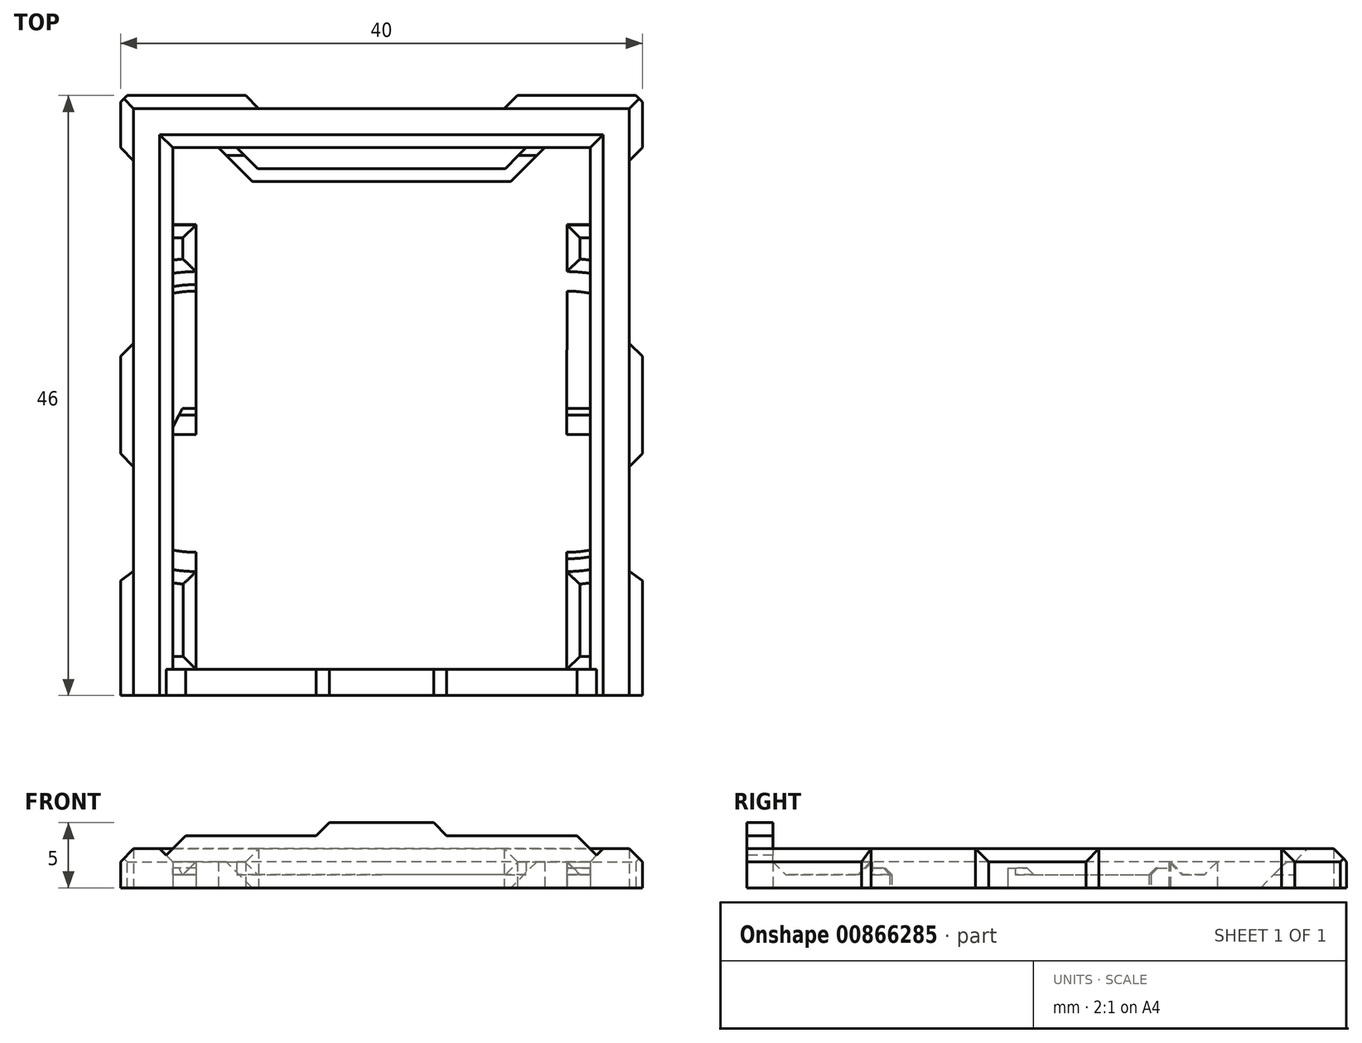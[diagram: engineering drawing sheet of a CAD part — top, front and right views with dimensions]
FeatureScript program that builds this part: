
annotation { "Feature Type Name" : "Feature", "Feature Type Description" : "" }
export const myFeature = defineFeature(function(context is Context, id is Id, definition is map)
    precondition{}
    {
        {
            var Q0;
            Q0=qCreatedBy(makeId("Top.planeOp"),FACE);
            var sketch = newSketch(context, id + "F0", { "sketchPlane" : qUnion([Q0])});
            skLineSegment(sketch, "E0", {"start": v(-16, -21) * mm, "end": v(-20, -21) * mm});
            skLineSegment(sketch, "E1", {"start": v(0, -19) * mm, "end": v(-16, -19) * mm});
            skLineSegment(sketch, "E2", {"start": v(-16, -21) * mm, "end": v(-16, -19) * mm});
            skLineSegment(sketch, "E3", {"start": v(-16, -19) * mm, "end": v(-16, 21) * mm});
            skLineSegment(sketch, "E4", {"start": v(-20, -21) * mm, "end": v(-20, -12.2) * mm});
            skLineSegment(sketch, "E5", {"start": v(-20, 21) * mm, "end": v(-20, 25) * mm});
            skLineSegment(sketch, "E6", {"start": v(-10.41, 25) * mm, "end": v(-20, 25) * mm});
            skLineSegment(sketch, "E7", {"start": v(-10.41, 25) * mm, "end": v(-9.41, 24) * mm});
            skLineSegment(sketch, "E8", {"start": v(-20, -12.2) * mm, "end": v(-19, -11.46) * mm});
            skLineSegment(sketch, "E9", {"start": v(-20, 21) * mm, "end": v(-19, 20) * mm});
            skLineSegment(sketch, "E10", {"start": v(-19, -11.46) * mm, "end": v(-19, -3.46) * mm});
            skLineSegment(sketch, "E11", {"start": v(-20, 5) * mm, "end": v(-19, 6) * mm});
            skLineSegment(sketch, "E12", {"start": v(-20, -2.46) * mm, "end": v(-19, -3.46) * mm});
            skLineSegment(sketch, "E13", {"start": v(-20, 5) * mm, "end": v(-20, -2.46) * mm});
            skLineSegment(sketch, "E14", {"start": v(-19, 6) * mm, "end": v(-19, 20) * mm});
            skLineSegment(sketch, "E15", {"start": v(-16, -21) * mm, "end": v(-14, -21) * mm});
            skLineSegment(sketch, "E16", {"start": v(0, -21) * mm, "end": v(-5, -21) * mm});
            skLineSegment(sketch, "E17", {"start": v(-5, -21) * mm, "end": v(-5, -19) * mm});
            skPoint(sketch, "E18", {"position": v(-9.91, 24.5) * mm});
            skLineSegment(sketch, "E19", {"start": v(-9.5, 19.4) * mm, "end": v(-11.1, 21) * mm});
            skLineSegment(sketch, "E20", {"start": v(-9.91, 18.4) * mm, "end": v(-12.51, 21) * mm});
            skLineSegment(sketch, "E21", {"start": v(-9.91, 18.4) * mm, "end": v(0, 18.4) * mm});
            skPoint(sketch, "E22.middle", {"position": v(-14.2, -0.02) * mm});
            skLineSegment(sketch, "E23", {"start": v(-15.28, 1) * mm, "end": v(-14.2, 1) * mm});
            skLineSegment(sketch, "E24", {"start": v(-14.22, 15.09) * mm, "end": v(-14.22, 11.5) * mm});
            skLineSegment(sketch, "E25", {"start": v(-14.2, -11.5) * mm, "end": v(-14.2, -19) * mm});
            skLineSegment(sketch, "E26.0", {"start": v(-15.2, -12.46) * mm, "end": v(-15.2, -18) * mm});
            skLineSegment(sketch, "E26.6", {"start": v(-15.22, 14.08) * mm, "end": v(-15.22, 12.46) * mm});
            skPoint(sketch, "E27.endSnap0", {"position": v(-14.2, 10) * mm});
            skLineSegment(sketch, "E28", {"start": v(-14.2, -0.02) * mm, "end": v(-14.2, -11.5) * mm});
            skLineSegment(sketch, "E29", {"start": v(-14.2, -0.02) * mm, "end": v(-14.22, 11.5) * mm});
            skLineSegment(sketch, "E30", {"start": v(-14.22, 15.09) * mm, "end": v(-16, 15.09) * mm});
            skLineSegment(sketch, "E31", {"start": v(-15.22, 14.08) * mm, "end": v(-16, 14.08) * mm});
            skLineSegment(sketch, "E32", {"start": v(-15.2, -18) * mm, "end": v(-16, -18) * mm});
            skArc(sketch, "E33", {"start": v(-14.2, -11.5) * mm, "mid": v(-15.1, -11.46) * mm, "end": v(-16, -11.36) * mm});
            skArc(sketch, "E34", {"start": v(-14.22, 11.5) * mm, "mid": v(-15.11, 11.46) * mm, "end": v(-16, 11.36) * mm});
            skArc(sketch, "E35", {"start": v(-15.22, 12.46) * mm, "mid": v(-15.61, 12.42) * mm, "end": v(-16, 12.37) * mm});
            skArc(sketch, "E36", {"start": v(-15.2, -12.46) * mm, "mid": v(-15.6, -12.42) * mm, "end": v(-16, -12.37) * mm});
            skLineSegment(sketch, "E37", {"start": v(-15.28, 1) * mm, "end": v(-16, 1) * mm});
            skLineSegment(sketch, "E38", {"start": v(-15.28, 1) * mm, "end": v(-16, -0.43) * mm});
            skLineSegment(sketch, "E39", {"start": v(-14.2, -1) * mm, "end": v(-16, -1) * mm});
            skArc(sketch, "E40", {"start": v(-14.2, 10) * mm, "mid": v(-15.1, 9.96) * mm, "end": v(-16, 9.84) * mm});
            skArc(sketch, "E41", {"start": v(-14.2, -10.02) * mm, "mid": v(-15.1, -9.98) * mm, "end": v(-16, -9.86) * mm});
            skLineSegment(sketch, "E42", {"start": v(-14.2, -1) * mm, "end": v(-14.2, 1) * mm});
            skLineSegment(sketch, "E43", {"start": v(-16, -1) * mm, "end": v(-14.2, -1) * mm});
            skLineSegment(sketch, "E44", {"start": v(-9.5, 19.4) * mm, "end": v(0, 19.4) * mm});
            skLineSegment(sketch, "E45", {"start": v(-16, 21) * mm, "end": v(0, 21) * mm});
            skLineSegment(sketch, "E46", {"start": v(-9.41, 24) * mm, "end": v(0, 24) * mm});
            skLineSegment(sketch, "E47", {"start": v(-14, -21) * mm, "end": v(-5, -21) * mm});
            skLineSegment(sketch, "E48.MirrorCS", {"start": v(14.2, -1) * mm, "end": v(14.2, 1) * mm});
            skLineSegment(sketch, "E49.MirrorCS", {"start": v(15.28, 1) * mm, "end": v(16, 1) * mm});
            skLineSegment(sketch, "E50.MirrorCS", {"start": v(15.28, 1) * mm, "end": v(14.2, 1) * mm});
            skLineSegment(sketch, "E51.MirrorCS", {"start": v(16, -1) * mm, "end": v(14.2, -1) * mm});
            skLineSegment(sketch, "E52.MirrorCS", {"start": v(16, -21) * mm, "end": v(16, -19) * mm});
            skLineSegment(sketch, "E53.MirrorCS", {"start": v(15.28, 1) * mm, "end": v(16, -0.43) * mm});
            skLineSegment(sketch, "E54.MirrorCS", {"start": v(10.41, 25) * mm, "end": v(9.41, 24) * mm});
            skLineSegment(sketch, "E55.MirrorCS", {"start": v(15.22, 14.08) * mm, "end": v(15.22, 12.46) * mm});
            skLineSegment(sketch, "E56.MirrorCS", {"start": v(16, -21) * mm, "end": v(14, -21) * mm});
            skLineSegment(sketch, "E57.MirrorCS", {"start": v(20, 5) * mm, "end": v(19, 6) * mm});
            skLineSegment(sketch, "E58.MirrorCS", {"start": v(14.2, -1) * mm, "end": v(16, -1) * mm});
            skLineSegment(sketch, "E59.MirrorCS", {"start": v(20, -2.46) * mm, "end": v(19, -3.46) * mm});
            skLineSegment(sketch, "E60.MirrorCS", {"start": v(20, -12.2) * mm, "end": v(19, -11.46) * mm});
            skArc(sketch, "E61.MirrorCS", {"start": v(14.22, 11.5) * mm, "mid": v(15.11, 11.46) * mm, "end": v(16, 11.36) * mm});
            skArc(sketch, "E62.MirrorCS", {"start": v(15.22, 12.46) * mm, "mid": v(15.61, 12.42) * mm, "end": v(16, 12.37) * mm});
            skArc(sketch, "E63.MirrorCS", {"start": v(15.2, -12.46) * mm, "mid": v(15.6, -12.42) * mm, "end": v(16, -12.37) * mm});
            skLineSegment(sketch, "E64.MirrorCS", {"start": v(15.22, 14.08) * mm, "end": v(16, 14.08) * mm});
            skLineSegment(sketch, "E65.MirrorCS", {"start": v(14.22, 15.09) * mm, "end": v(16, 15.09) * mm});
            skLineSegment(sketch, "E66.MirrorCS", {"start": v(14.22, 15.09) * mm, "end": v(14.22, 11.5) * mm});
            skLineSegment(sketch, "E67.MirrorCS", {"start": v(15.2, -18) * mm, "end": v(16, -18) * mm});
            skLineSegment(sketch, "E68.MirrorCS", {"start": v(20, 21) * mm, "end": v(19, 20) * mm});
            skLineSegment(sketch, "E69.MirrorCS", {"start": v(9.5, 19.4) * mm, "end": v(11.1, 21) * mm});
            skArc(sketch, "E70.MirrorCS", {"start": v(14.2, -11.5) * mm, "mid": v(15.1, -11.46) * mm, "end": v(16, -11.36) * mm});
            skArc(sketch, "E71.MirrorCS", {"start": v(14.2, -10.02) * mm, "mid": v(15.1, -9.98) * mm, "end": v(16, -9.86) * mm});
            skLineSegment(sketch, "E72.MirrorCS", {"start": v(5, -21) * mm, "end": v(5, -19) * mm});
            skArc(sketch, "E73.MirrorCS", {"start": v(14.2, 10) * mm, "mid": v(15.1, 9.96) * mm, "end": v(16, 9.84) * mm});
            skPoint(sketch, "E74.MirrorP", {"position": v(14.2, 10) * mm});
            skLineSegment(sketch, "E75.MirrorCS", {"start": v(15.2, -12.46) * mm, "end": v(15.2, -18) * mm});
            skLineSegment(sketch, "E76.MirrorCS", {"start": v(19, 6) * mm, "end": v(19, 20) * mm});
            skLineSegment(sketch, "E77.MirrorCS", {"start": v(9.5, 19.4) * mm, "end": v(0, 19.4) * mm});
            skLineSegment(sketch, "E78.MirrorCS", {"start": v(16, -21) * mm, "end": v(20, -21) * mm});
            skLineSegment(sketch, "E79.MirrorCS", {"start": v(14.2, -0.02) * mm, "end": v(14.22, 11.5) * mm});
            skLineSegment(sketch, "E80.MirrorCS", {"start": v(10.41, 25) * mm, "end": v(20, 25) * mm});
            skLineSegment(sketch, "E81.MirrorCS", {"start": v(19, -11.46) * mm, "end": v(19, -3.46) * mm});
            skLineSegment(sketch, "E82.MirrorCS", {"start": v(20, 5) * mm, "end": v(20, -2.46) * mm});
            skLineSegment(sketch, "E83.MirrorCS", {"start": v(14, -21) * mm, "end": v(5, -21) * mm});
            skLineSegment(sketch, "E84.MirrorCS", {"start": v(0, -21) * mm, "end": v(5, -21) * mm});
            skLineSegment(sketch, "E85.MirrorCS", {"start": v(16, -19) * mm, "end": v(16, 21) * mm});
            skLineSegment(sketch, "E86.MirrorCS", {"start": v(9.91, 18.4) * mm, "end": v(12.51, 21) * mm});
            skLineSegment(sketch, "E87.MirrorCS", {"start": v(9.91, 18.4) * mm, "end": v(0, 18.4) * mm});
            skLineSegment(sketch, "E88.MirrorCS", {"start": v(20, -21) * mm, "end": v(20, -12.2) * mm});
            skLineSegment(sketch, "E89.MirrorCS", {"start": v(16, 21) * mm, "end": v(0, 21) * mm});
            skPoint(sketch, "E90.MirrorP", {"position": v(9.91, 24.5) * mm});
            skLineSegment(sketch, "E91.MirrorCS", {"start": v(9.41, 24) * mm, "end": v(0, 24) * mm});
            skLineSegment(sketch, "E92.MirrorCS", {"start": v(20, 21) * mm, "end": v(20, 25) * mm});
            skLineSegment(sketch, "E93.MirrorCS", {"start": v(14.2, -0.02) * mm, "end": v(14.2, -11.5) * mm});
            skLineSegment(sketch, "E94.MirrorCS", {"start": v(14.2, -11.5) * mm, "end": v(14.2, -19) * mm});
            skLineSegment(sketch, "E95.MirrorCS", {"start": v(0, -19) * mm, "end": v(16, -19) * mm});
            skSolve(sketch);
        }
        {
            var Q0;
            Q0=makeQuery(id+"F0.imprint","IMPRINT",FACE,{"disambiguationData":[TD([[makeQuery(id+"F0.imprint","IMPRINT",EDGE,{"derivedFrom":sQuery(id+"F0.wireOp",EDGE,"E0")}),-1.0]])]});
            extrude(context, id + "F1", {"entities" : qUnion([Q0]), "depth" : 3 * mm, "offsetDistance" : 25 * mm});
        }
        {
            var Q0;
            {var subQ0=sQuery(id+"F0.wireOp",EDGE,"E2");Q0=makeQuery(id+"F0.imprint","IMPRINT",FACE,{"disambiguationData":[TD([[makeQuery(id+"F0.imprint","IMPRINT",EDGE,{"derivedFrom":subQ0}),-1.0]])]});}
            var Q1;
            {var subQ1=sQuery(id+"F0.wireOp",EDGE,"E52.MirrorCS");Q1=makeQuery(id+"F0.imprint","IMPRINT",FACE,{"disambiguationData":[TD([[makeQuery(id+"F0.imprint","IMPRINT",EDGE,{"derivedFrom":subQ1}),1.0]])]});}
            extrude(context, id + "F2", {"entities" : qUnion([Q0, Q1]), "operationType" : NewBodyOperationType.ADD, "depth" : 4 * mm, "offsetDistance" : 25 * mm});
        }
        {
            var Q0;
            Q0=makeQuery(id+"F0.imprint","IMPRINT",FACE,{"disambiguationData":[TD([[makeQuery(id+"F0.imprint","IMPRINT",EDGE,{"derivedFrom":sQuery(id+"F0.wireOp",EDGE,"E16")}),-1.0]])]});
            extrude(context, id + "F3", {"entities" : qUnion([Q0]), "operationType" : NewBodyOperationType.ADD, "depth" : 5 * mm, "offsetDistance" : 25 * mm});
        }
        {
            var Q0;
            {var subQ0=sQuery(id+"F0.wireOp",EDGE,"E25");Q0=makeQuery(id+"F0.imprint","IMPRINT",FACE,{"disambiguationData":[TD([[makeQuery(id+"F0.imprint","IMPRINT",EDGE,{"derivedFrom":subQ0}),-1.0]])]});}
            var Q1;
            {var subQ0=sQuery(id+"F0.wireOp",EDGE,"E63.MirrorCS");Q1=makeQuery(id+"F0.imprint","IMPRINT",FACE,{"disambiguationData":[TD([[makeQuery(id+"F0.imprint","IMPRINT",EDGE,{"derivedFrom":subQ0}),1.0]])]});}
            var Q2;
            Q2=makeQuery(id+"F0.imprint","IMPRINT",FACE,{"disambiguationData":[TD([[makeQuery(id+"F0.imprint","IMPRINT",EDGE,{"derivedFrom":sQuery(id+"F0.wireOp",EDGE,"E55.MirrorCS")}),-1.0]])]});
            var Q3;
            Q3=makeQuery(id+"F0.imprint","IMPRINT",FACE,{"disambiguationData":[TD([[makeQuery(id+"F0.imprint","IMPRINT",EDGE,{"derivedFrom":sQuery(id+"F0.wireOp",EDGE,"E24")}),-1.0]])]});
            var Q4;
            {var subQ2=sQuery(id+"F0.wireOp",EDGE,"E19");Q4=makeQuery(id+"F0.imprint","IMPRINT",FACE,{"disambiguationData":[TD([[makeQuery(id+"F0.imprint","IMPRINT",EDGE,{"derivedFrom":subQ2}),1.0]])]});}
            extrude(context, id + "F4", {"entities" : qUnion([Q0, Q1, Q2, Q3, Q4]), "operationType" : NewBodyOperationType.ADD, "depth" : 2 * mm, "offsetDistance" : 25 * mm});
        }
        {
            var Q0;
            {var subQ0=sQuery(id+"F0.wireOp",EDGE,"E33");Q0=makeQuery(id+"F0.imprint","IMPRINT",FACE,{"disambiguationData":[TD([[makeQuery(id+"F0.imprint","IMPRINT",EDGE,{"derivedFrom":subQ0}),-1.0]])]});}
            var Q1;
            {var subQ0=sQuery(id+"F0.wireOp",EDGE,"E34");Q1=makeQuery(id+"F0.imprint","IMPRINT",FACE,{"disambiguationData":[TD([[makeQuery(id+"F0.imprint","IMPRINT",EDGE,{"derivedFrom":subQ0}),1.0]])]});}
            var Q2;
            Q2=makeQuery(id+"F0.imprint","IMPRINT",FACE,{"disambiguationData":[TD([[makeQuery(id+"F0.imprint","IMPRINT",EDGE,{"derivedFrom":sQuery(id+"F0.wireOp",EDGE,"E23")}),-1.0]])]});
            var Q3;
            {var subQ0=sQuery(id+"F0.wireOp",EDGE,"E70.MirrorCS");Q3=makeQuery(id+"F0.imprint","IMPRINT",FACE,{"disambiguationData":[TD([[makeQuery(id+"F0.imprint","IMPRINT",EDGE,{"derivedFrom":subQ0}),1.0]])]});}
            var Q4;
            {var subQ0=sQuery(id+"F0.wireOp",EDGE,"E61.MirrorCS");Q4=makeQuery(id+"F0.imprint","IMPRINT",FACE,{"disambiguationData":[TD([[makeQuery(id+"F0.imprint","IMPRINT",EDGE,{"derivedFrom":subQ0}),-1.0]])]});}
            var Q5;
            Q5=makeQuery(id+"F0.imprint","IMPRINT",FACE,{"disambiguationData":[TD([[makeQuery(id+"F0.imprint","IMPRINT",EDGE,{"derivedFrom":sQuery(id+"F0.wireOp",EDGE,"E48.MirrorCS")}),-1.0]])]});
            var Q6;
            {var subQ0=sQuery(id+"F0.wireOp",EDGE,"E49.MirrorCS");Q6=makeQuery(id+"F0.imprint","IMPRINT",FACE,{"disambiguationData":[TD([[makeQuery(id+"F0.imprint","IMPRINT",EDGE,{"derivedFrom":subQ0}),-1.0]])]});}
            extrude(context, id + "F5", {"entities" : qUnion([Q0, Q1, Q2, Q3, Q4, Q5, Q6]), "operationType" : NewBodyOperationType.ADD, "depth" : 1.5 * mm, "offsetDistance" : 25 * mm});
        }
        {
            var Q0;
            Q0=makeQuery(id+"F0.imprint","IMPRINT",FACE,{"disambiguationData":[TD([[makeQuery(id+"F0.imprint","IMPRINT",EDGE,{"derivedFrom":sQuery(id+"F0.wireOp",EDGE,"E26.0")}),-1.0]])]});
            var Q1;
            {var subQ0=sQuery(id+"F0.wireOp",EDGE,"E41");Q1=makeQuery(id+"F0.imprint","IMPRINT",FACE,{"disambiguationData":[TD([[makeQuery(id+"F0.imprint","IMPRINT",EDGE,{"derivedFrom":subQ0}),-1.0]])]});}
            var Q2;
            {var subQ0=sQuery(id+"F0.wireOp",EDGE,"E37");Q2=makeQuery(id+"F0.imprint","IMPRINT",FACE,{"disambiguationData":[TD([[makeQuery(id+"F0.imprint","IMPRINT",EDGE,{"derivedFrom":subQ0}),1.0]])]});}
            var Q3;
            Q3=makeQuery(id+"F0.imprint","IMPRINT",FACE,{"disambiguationData":[TD([[makeQuery(id+"F0.imprint","IMPRINT",EDGE,{"derivedFrom":sQuery(id+"F0.wireOp",EDGE,"E23")}),1.0]])]});
            var Q4;
            Q4=makeQuery(id+"F0.imprint","IMPRINT",FACE,{"disambiguationData":[TD([[makeQuery(id+"F0.imprint","IMPRINT",EDGE,{"derivedFrom":sQuery(id+"F0.wireOp",EDGE,"E26.6")}),-1.0]])]});
            var Q5;
            {var subQ2=sQuery(id+"F0.wireOp",EDGE,"E19");Q5=makeQuery(id+"F0.imprint","IMPRINT",FACE,{"disambiguationData":[TD([[makeQuery(id+"F0.imprint","IMPRINT",EDGE,{"derivedFrom":subQ2}),-1.0]])]});}
            var Q6;
            Q6=makeQuery(id+"F0.imprint","IMPRINT",FACE,{"disambiguationData":[TD([[makeQuery(id+"F0.imprint","IMPRINT",EDGE,{"derivedFrom":sQuery(id+"F0.wireOp",EDGE,"E55.MirrorCS")}),1.0]])]});
            var Q7;
            {var subQ6=sQuery(id+"F0.wireOp",EDGE,"E48.MirrorCS");Q7=makeQuery(id+"F0.imprint","IMPRINT",FACE,{"disambiguationData":[TD([[makeQuery(id+"F0.imprint","IMPRINT",EDGE,{"derivedFrom":subQ6}),1.0]])]});}
            var Q8;
            {var subQ0=sQuery(id+"F0.wireOp",EDGE,"E58.MirrorCS");Q8=makeQuery(id+"F0.imprint","IMPRINT",FACE,{"disambiguationData":[TD([[makeQuery(id+"F0.imprint","IMPRINT",EDGE,{"derivedFrom":subQ0}),-1.0]])]});}
            var Q9;
            {var subQ0=sQuery(id+"F0.wireOp",EDGE,"E63.MirrorCS");Q9=makeQuery(id+"F0.imprint","IMPRINT",FACE,{"disambiguationData":[TD([[makeQuery(id+"F0.imprint","IMPRINT",EDGE,{"derivedFrom":subQ0}),-1.0]])]});}
            extrude(context, id + "F6", {"entities" : qUnion([Q0, Q1, Q2, Q3, Q4, Q5, Q6, Q7, Q8, Q9]), "operationType" : NewBodyOperationType.ADD, "depth" : 1 * mm, "offsetDistance" : 25 * mm});
        }
        {
            var Q0;
            Q0=makeQuery(id+"F1.opExtrude","CAP_EDGE",EDGE,{"disambiguationData":[OSD([sQuery(id+"F0.wireOp",EDGE,"E80.MirrorCS")])],"isStart":false});
            var Q1;
            Q1=makeQuery(id+"F1.opExtrude","CAP_EDGE",EDGE,{"disambiguationData":[OSD([sQuery(id+"F0.wireOp",EDGE,"E92.MirrorCS")])],"isStart":false});
            var Q2;
            Q2=makeQuery(id+"F1.opExtrude","CAP_EDGE",EDGE,{"disambiguationData":[OSD([sQuery(id+"F0.wireOp",EDGE,"E82.MirrorCS")])],"isStart":false});
            var Q3;
            Q3=makeQuery(id+"F1.opExtrude","CAP_EDGE",EDGE,{"disambiguationData":[OSD([sQuery(id+"F0.wireOp",EDGE,"E88.MirrorCS")])],"isStart":false});
            var Q4;
            Q4=makeQuery(id+"F1.opExtrude","CAP_EDGE",EDGE,{"disambiguationData":[OSD([sQuery(id+"F0.wireOp",EDGE,"E6")])],"isStart":false});
            var Q5;
            Q5=makeQuery(id+"F1.opExtrude","CAP_EDGE",EDGE,{"disambiguationData":[OSD([sQuery(id+"F0.wireOp",EDGE,"E5")])],"isStart":false});
            var Q6;
            Q6=makeQuery(id+"F1.opExtrude","CAP_EDGE",EDGE,{"disambiguationData":[OSD([sQuery(id+"F0.wireOp",EDGE,"E13")])],"isStart":false});
            var Q7;
            Q7=makeQuery(id+"F1.opExtrude","CAP_EDGE",EDGE,{"disambiguationData":[OSD([sQuery(id+"F0.wireOp",EDGE,"E4")])],"isStart":false});
            var Q8;
            Q8=makeQuery(id+"F2.opExtrude","CAP_EDGE",EDGE,{"disambiguationData":[OSD([sQuery(id+"F0.wireOp",EDGE,"E52.MirrorCS")])],"isStart":false});
            var Q9;
            Q9=makeQuery(id+"F3.opExtrude","CAP_EDGE",EDGE,{"disambiguationData":[OSD([sQuery(id+"F0.wireOp",EDGE,"E72.MirrorCS")])],"isStart":false});
            var Q10;
            Q10=makeQuery(id+"F3.opExtrude","CAP_EDGE",EDGE,{"disambiguationData":[OSD([sQuery(id+"F0.wireOp",EDGE,"E17")])],"isStart":false});
            var Q11;
            Q11=makeQuery(id+"F2.opExtrude","CAP_EDGE",EDGE,{"disambiguationData":[OSD([sQuery(id+"F0.wireOp",EDGE,"E2")])],"isStart":false});
            chamfer(context, id + "F7", {"entities" : qUnion([Q0, Q1, Q2, Q3, Q4, Q5, Q6, Q7, Q8, Q9, Q10, Q11]), "width" : 1 * mm, "tangentPropagation" : true});
        }
        {
            var Q0;
            Q0=makeQuery(id+"F1.opExtrude","SWEPT_EDGE",EDGE,{"disambiguationData":[OSD([sQuery(id+"F0.wireOp",EDGE,"E80.MirrorCS"),sQuery(id+"F0.wireOp",EDGE,"E92.MirrorCS")])]});
            var Q1;
            Q1=makeQuery(id+"F1.opExtrude","SWEPT_EDGE",EDGE,{"disambiguationData":[OSD([sQuery(id+"F0.wireOp",EDGE,"E5"),sQuery(id+"F0.wireOp",EDGE,"E6")])]});
            chamfer(context, id + "F8", {"entities" : qUnion([Q0, Q1]), "width" : .5 * mm, "tangentPropagation" : true});
        }
        {
            var Q0;
            Q0=makeQuery(id+"F4.opExtrude","CAP_EDGE",EDGE,{"disambiguationData":[OSD([sQuery(id+"F0.wireOp",EDGE,"E36")])],"isStart":false});
            var Q1;
            Q1=makeQuery(id+"F4.opExtrude","CAP_EDGE",EDGE,{"disambiguationData":[OSD([sQuery(id+"F0.wireOp",EDGE,"E26.0")])],"isStart":false});
            var Q2;
            Q2=makeQuery(id+"F4.opExtrude","CAP_EDGE",EDGE,{"disambiguationData":[OSD([sQuery(id+"F0.wireOp",EDGE,"E32")])],"isStart":false});
            var Q3;
            Q3=makeQuery(id+"F4.opExtrude","CAP_EDGE",EDGE,{"disambiguationData":[OSD([sQuery(id+"F0.wireOp",EDGE,"E63.MirrorCS")])],"isStart":false});
            var Q4;
            Q4=makeQuery(id+"F4.opExtrude","CAP_EDGE",EDGE,{"disambiguationData":[OSD([sQuery(id+"F0.wireOp",EDGE,"E75.MirrorCS")])],"isStart":false});
            var Q5;
            Q5=makeQuery(id+"F4.opExtrude","CAP_EDGE",EDGE,{"disambiguationData":[OSD([sQuery(id+"F0.wireOp",EDGE,"E67.MirrorCS")])],"isStart":false});
            var Q6;
            Q6=makeQuery(id+"F4.opExtrude","CAP_EDGE",EDGE,{"disambiguationData":[OSD([sQuery(id+"F0.wireOp",EDGE,"E62.MirrorCS")])],"isStart":false});
            var Q7;
            Q7=makeQuery(id+"F4.opExtrude","CAP_EDGE",EDGE,{"disambiguationData":[OSD([sQuery(id+"F0.wireOp",EDGE,"E55.MirrorCS")])],"isStart":false});
            var Q8;
            Q8=makeQuery(id+"F4.opExtrude","CAP_EDGE",EDGE,{"disambiguationData":[OSD([sQuery(id+"F0.wireOp",EDGE,"E64.MirrorCS")])],"isStart":false});
            var Q9;
            Q9=makeQuery(id+"F4.opExtrude","CAP_EDGE",EDGE,{"disambiguationData":[OSD([sQuery(id+"F0.wireOp",EDGE,"E31")])],"isStart":false});
            var Q10;
            Q10=makeQuery(id+"F4.opExtrude","CAP_EDGE",EDGE,{"disambiguationData":[OSD([sQuery(id+"F0.wireOp",EDGE,"E26.6")])],"isStart":false});
            var Q11;
            Q11=makeQuery(id+"F4.opExtrude","CAP_EDGE",EDGE,{"disambiguationData":[OSD([sQuery(id+"F0.wireOp",EDGE,"E35")])],"isStart":false});
            chamfer(context, id + "F9", {"entities" : qUnion([Q0, Q1, Q2, Q3, Q4, Q5, Q6, Q7, Q8, Q9, Q10, Q11]), "width" : 1 * mm, "tangentPropagation" : true});
        }
        {
            var Q0;
            Q0=makeQuery(id+"F5.opExtrude","CAP_EDGE",EDGE,{"disambiguationData":[OSD([sQuery(id+"F0.wireOp",EDGE,"E40")])],"isStart":false});
            var Q1;
            Q1=makeQuery(id+"F5.opExtrude","CAP_EDGE",EDGE,{"disambiguationData":[OSD([sQuery(id+"F0.wireOp",EDGE,"E73.MirrorCS")])],"isStart":false});
            var Q2;
            Q2=makeQuery(id+"F5.opExtrude","CAP_EDGE",EDGE,{"disambiguationData":[OSD([sQuery(id+"F0.wireOp",EDGE,"E41")])],"isStart":false});
            var Q3;
            Q3=makeQuery(id+"F5.opExtrude","CAP_EDGE",EDGE,{"disambiguationData":[OSD([sQuery(id+"F0.wireOp",EDGE,"E71.MirrorCS")])],"isStart":false});
            var Q4;
            Q4=makeQuery(id+"F5.opExtrude","CAP_EDGE",EDGE,{"disambiguationData":[OSD([sQuery(id+"F0.wireOp",EDGE,"E43")])],"isStart":false});
            var Q5;
            Q5=makeQuery(id+"F5.opExtrude","CAP_EDGE",EDGE,{"disambiguationData":[OSD([sQuery(id+"F0.wireOp",EDGE,"E58.MirrorCS")])],"isStart":false});
            var Q6;
            Q6=makeQuery(id+"F5.opExtrude","CAP_EDGE",EDGE,{"disambiguationData":[OSD([sQuery(id+"F0.wireOp",EDGE,"E23")])],"isStart":false});
            var Q7;
            Q7=makeQuery(id+"F5.opExtrude","CAP_EDGE",EDGE,{"disambiguationData":[OSD([sQuery(id+"F0.wireOp",EDGE,"E38")])],"isStart":false});
            var Q8;
            Q8=makeQuery(id+"F5.opExtrude","CAP_EDGE",EDGE,{"disambiguationData":[OSD([sQuery(id+"F0.wireOp",EDGE,"E50.MirrorCS")])],"isStart":false});
            chamfer(context, id + "F10", {"entities" : qUnion([Q0, Q1, Q2, Q3, Q4, Q5, Q6, Q7, Q8]), "width" : .5 * mm, "tangentPropagation" : true});
        }
        {
            var Q0;
            Q0=makeQuery(id+"F4.opExtrude","CAP_EDGE",EDGE,{"disambiguationData":[OSD([sQuery(id+"F0.wireOp",EDGE,"E21"),sQuery(id+"F0.wireOp",EDGE,"E87.MirrorCS")])],"isStart":false});
            chamfer(context, id + "F11", {"entities" : qUnion([Q0]), "width" : 2 * mm, "tangentPropagation" : true});
        }
        {
            var Q0;
            Q0=makeQuery(id+"F1.opExtrude","CAP_EDGE",EDGE,{"disambiguationData":[OSD([sQuery(id+"F0.wireOp",EDGE,"E3")])],"isStart":false});
            var Q1;
            Q1=makeQuery(id+"F1.opExtrude","CAP_EDGE",EDGE,{"disambiguationData":[OSD([sQuery(id+"F0.wireOp",EDGE,"E45")])],"isStart":false});
            var Q2;
            Q2=makeQuery(id+"F1.opExtrude","CAP_EDGE",EDGE,{"disambiguationData":[OSD([sQuery(id+"F0.wireOp",EDGE,"E89.MirrorCS")])],"isStart":false});
            var Q3;
            Q3=makeQuery(id+"F1.opExtrude","CAP_EDGE",EDGE,{"disambiguationData":[OSD([sQuery(id+"F0.wireOp",EDGE,"E85.MirrorCS")])],"isStart":false});
            chamfer(context, id + "F12", {"entities" : qUnion([Q0, Q1, Q2, Q3]), "width" : 1 * mm, "tangentPropagation" : true});
        }
    });
